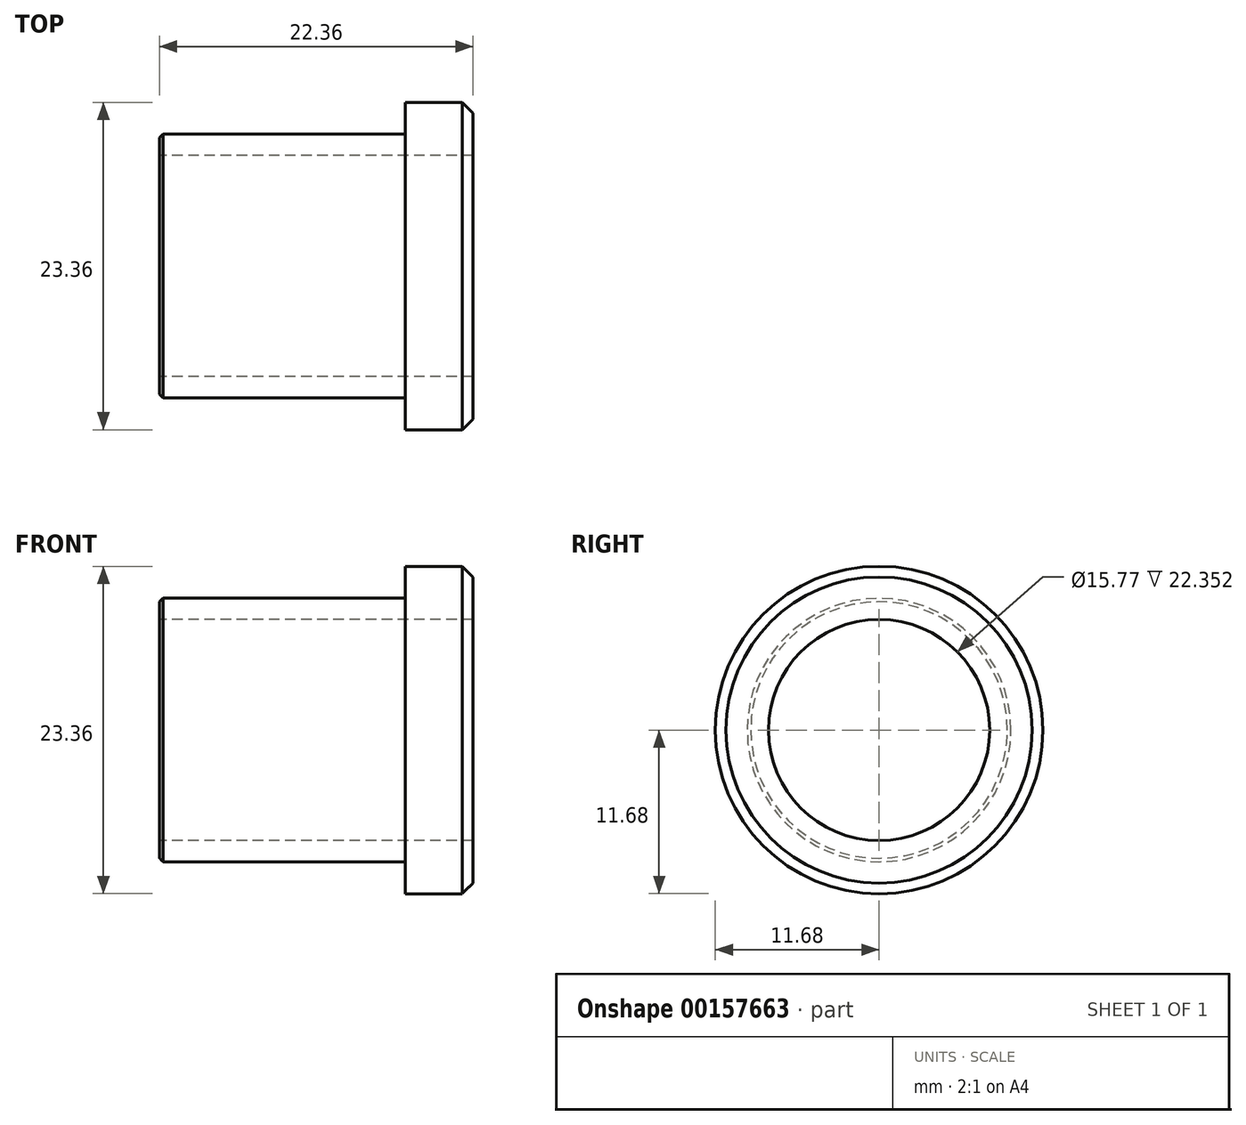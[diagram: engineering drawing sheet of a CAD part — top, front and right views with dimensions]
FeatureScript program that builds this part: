
annotation { "Feature Type Name" : "Feature", "Feature Type Description" : "" }
export const myFeature = defineFeature(function(context is Context, id is Id, definition is map)
    precondition{}
    {
        {
            var Q0;
            Q0=qCreatedBy(makeId("Right.planeOp"),FACE);
            var sketch = newSketch(context, id + "F0", { "sketchPlane" : qUnion([Q0])});
            skCircle(sketch, "E0", {"center": v(0, 0) * mm, "radius": 9.4 * mm});
            skCircle(sketch, "E1", {"center": v(0, 0) * mm, "radius": 11.68 * mm});
            skCircle(sketch, "E2", {"center": v(0, 0) * mm, "radius": 7.89 * mm});
            skSolve(sketch);
        }
        {
            var Q0;
            Q0=makeQuery(id+"F0.imprint","IMPRINT",FACE,{"disambiguationData":[TD([[makeQuery(id+"F0.imprint","IMPRINT",EDGE,{"derivedFrom":sQuery(id+"F0.wireOp",EDGE,"E0")}),1.0]])]});
            var Q1;
            Q1=makeQuery(id+"F0.imprint","IMPRINT",FACE,{"disambiguationData":[TD([[makeQuery(id+"F0.imprint","IMPRINT",EDGE,{"derivedFrom":sQuery(id+"F0.wireOp",EDGE,"E0")}),-1.0]])]});
            extrude(context, id + "F1", {"entities" : qUnion([Q0, Q1]), "depth" : 4.83 * mm});
        }
        {
            var Q0;
            Q0=makeQuery(id+"F0.imprint","IMPRINT",FACE,{"disambiguationData":[TD([[makeQuery(id+"F0.imprint","IMPRINT",EDGE,{"derivedFrom":sQuery(id+"F0.wireOp",EDGE,"E0")}),1.0]])]});
            extrude(context, id + "F2", {"entities" : qUnion([Q0]), "operationType" : NewBodyOperationType.ADD, "oppositeDirection" : true, "depth" : 17.53 * mm});
        }
        {
            var Q0;
            Q0=makeQuery(id+"F1.opExtrude","CAP_EDGE",EDGE,{"disambiguationData":[OSD([sQuery(id+"F0.wireOp",EDGE,"E1")])],"isStart":false});
            chamfer(context, id + "F3", {"entities" : qUnion([Q0]), "width" : 0.76 * mm, "tangentPropagation" : true});
        }
        {
            var Q0;
            Q0=makeQuery(id+"F2.opExtrude","CAP_EDGE",EDGE,{"disambiguationData":[OSD([sQuery(id+"F0.wireOp",EDGE,"E0")])],"isStart":false});
            chamfer(context, id + "F4", {"entities" : qUnion([Q0]), "width" : 0.25 * mm, "tangentPropagation" : true});
        }
    });
